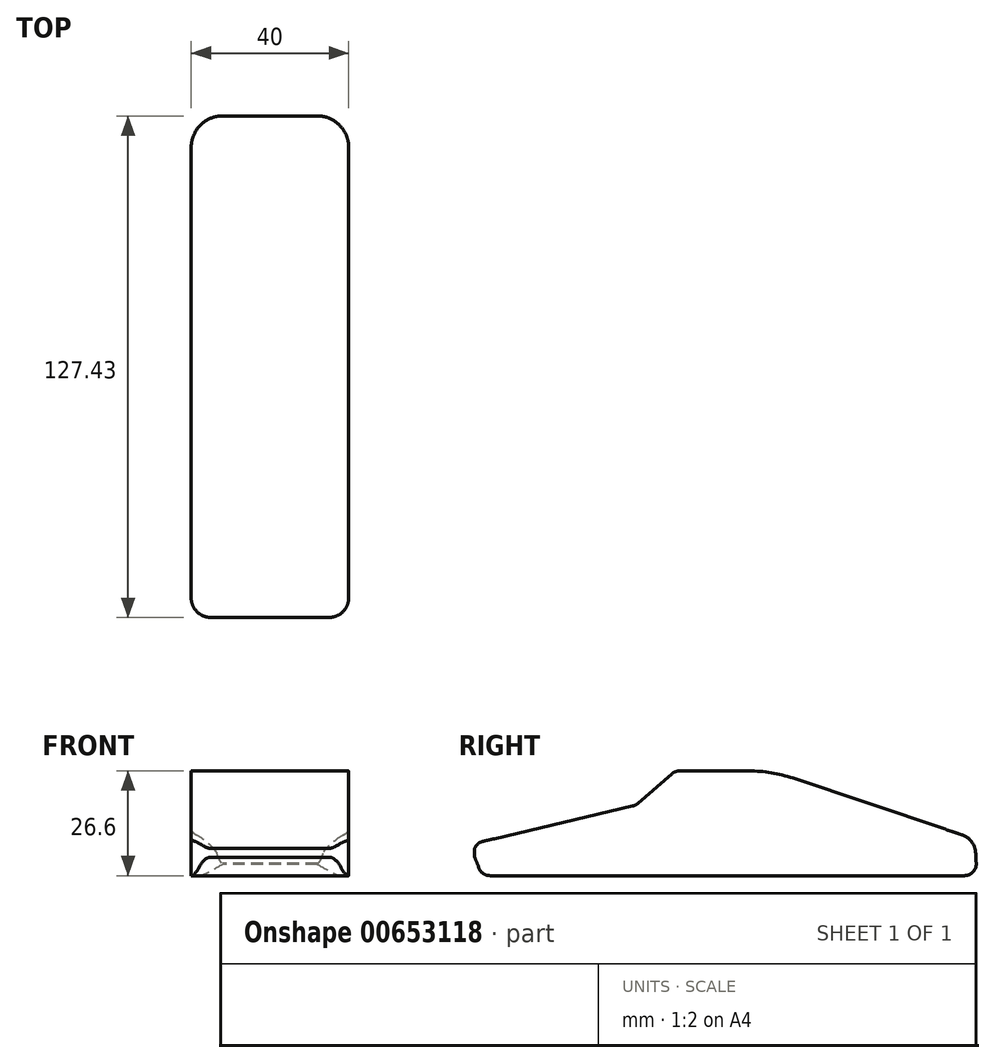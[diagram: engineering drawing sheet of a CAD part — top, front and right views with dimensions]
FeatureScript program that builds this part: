
annotation { "Feature Type Name" : "Feature", "Feature Type Description" : "" }
export const myFeature = defineFeature(function(context is Context, id is Id, definition is map)
    precondition{}
    {
        {
            var Q0;
            Q0=qCreatedBy(makeId("Right.planeOp"),FACE);
            var sketch = newSketch(context, id + "F0", { "sketchPlane" : qUnion([Q0])});
            skLineSegment(sketch, "E0", {"start": v(-61.53, 7.56) * mm, "end": v(59.02, 7.56) * mm});
            skLineSegment(sketch, "E1", {"start": v(62.01, 10.73) * mm, "end": v(61.85, 13.44) * mm});
            skLineSegment(sketch, "E2", {"start": v(58.45, 17.9) * mm, "end": v(15.44, 32.34) * mm});
            skLineSegment(sketch, "E3", {"start": v(4.3, 34.16) * mm, "end": v(-13.37, 34.16) * mm});
            skLineSegment(sketch, "E4", {"start": v(-15.34, 33.42) * mm, "end": v(-23.98, 25.9) * mm});
            skLineSegment(sketch, "E5", {"start": v(-25.26, 25.25) * mm, "end": v(-63.32, 16.27) * mm});
            skLineSegment(sketch, "E6", {"start": v(-65.42, 12.25) * mm, "end": v(-64.32, 9.46) * mm});
            skPoint(sketch, "E7.visualSharp", {"position": v(10.02, 34.16) * mm});
            skArc(sketch, "E7.filletArc", {"start": v(15.44, 32.34) * mm, "mid": v(9.94, 33.7) * mm, "end": v(4.3, 34.16) * mm});
            skPoint(sketch, "E8.visualSharp", {"position": v(61.66, 16.82) * mm});
            skArc(sketch, "E8.filletArc", {"start": v(61.85, 13.44) * mm, "mid": v(60.84, 16.19) * mm, "end": v(58.45, 17.9) * mm});
            skPoint(sketch, "E9.visualSharp", {"position": v(-66.7, 15.47) * mm});
            skArc(sketch, "E9.filletArc", {"start": v(-63.32, 16.27) * mm, "mid": v(-65.29, 14.74) * mm, "end": v(-65.42, 12.25) * mm});
            skPoint(sketch, "E10.visualSharp", {"position": v(-14.5, 34.16) * mm});
            skArc(sketch, "E10.filletArc", {"start": v(-13.37, 34.16) * mm, "mid": v(-14.42, 33.97) * mm, "end": v(-15.34, 33.42) * mm});
            skPoint(sketch, "E11.visualSharp", {"position": v(-24.54, 25.42) * mm});
            skArc(sketch, "E11.filletArc", {"start": v(-25.26, 25.25) * mm, "mid": v(-24.58, 25.5) * mm, "end": v(-23.98, 25.9) * mm});
            skPoint(sketch, "E12.visualSharp", {"position": v(-63.57, 7.56) * mm});
            skArc(sketch, "E12.filletArc", {"start": v(-64.32, 9.46) * mm, "mid": v(-63.22, 8.08) * mm, "end": v(-61.53, 7.56) * mm});
            skPoint(sketch, "E13.visualSharp", {"position": v(62.2, 7.56) * mm});
            skArc(sketch, "E13.filletArc", {"start": v(59.02, 7.56) * mm, "mid": v(61.2, 8.5) * mm, "end": v(62.01, 10.73) * mm});
            skSolve(sketch);
        }
        {
            var Q0;
            Q0=makeQuery(id+"F0.imprint","IMPRINT",FACE,{"disambiguationData":[TD([[makeQuery(id+"F0.imprint","IMPRINT",EDGE,{"derivedFrom":sQuery(id+"F0.wireOp",EDGE,"E0")}),1.0]])]});
            extrude(context, id + "F1", {"entities" : qUnion([Q0]), "depth" : 20 * mm, "offsetDistance" : 25.4 * mm, "hasSecondDirection" : true, "secondDirectionOppositeDirection" : true, "secondDirectionDepth" : 20 * mm});
        }
        {
            var Q0;
            Q0=qCreatedBy(makeId("Top.planeOp"),FACE);
            var sketch = newSketch(context, id + "F2", { "sketchPlane" : qUnion([Q0])});
            skLineSegment(sketch, "E14.bottom", {"start": v(-12, 62.01) * mm, "end": v(12, 62.01) * mm});
            skLineSegment(sketch, "E14.top", {"start": v(-15, -65.42) * mm, "end": v(15, -65.42) * mm});
            skLineSegment(sketch, "E14.left", {"start": v(-20, 54.01) * mm, "end": v(-20, -60.42) * mm});
            skLineSegment(sketch, "E14.right", {"start": v(20, 54.01) * mm, "end": v(20, -60.42) * mm});
            skPoint(sketch, "E15.visualSharp", {"position": v(-20, 62.01) * mm});
            skArc(sketch, "E15.filletArc", {"start": v(-12, 62.01) * mm, "mid": v(-17.66, 59.67) * mm, "end": v(-20, 54.01) * mm});
            skPoint(sketch, "E16.visualSharp", {"position": v(20, 62.01) * mm});
            skArc(sketch, "E16.filletArc", {"start": v(20, 54.01) * mm, "mid": v(17.66, 59.67) * mm, "end": v(12, 62.01) * mm});
            skPoint(sketch, "E17.visualSharp", {"position": v(-20, -65.42) * mm});
            skArc(sketch, "E17.filletArc", {"start": v(-20, -60.42) * mm, "mid": v(-18.54, -63.96) * mm, "end": v(-15, -65.42) * mm});
            skPoint(sketch, "E18.visualSharp", {"position": v(20, -65.42) * mm});
            skArc(sketch, "E18.filletArc", {"start": v(15, -65.42) * mm, "mid": v(18.54, -63.96) * mm, "end": v(20, -60.42) * mm});
            skSolve(sketch);
        }
        {
            var Q0;
            Q0 = qSketchRegion(id + "F2", true);
            extrude(context, id + "F3", {"entities" : qUnion([Q0]), "operationType" : NewBodyOperationType.INTERSECT, "depth" : 76.2 * mm, "offsetDistance" : 25.4 * mm});
        }
    });
